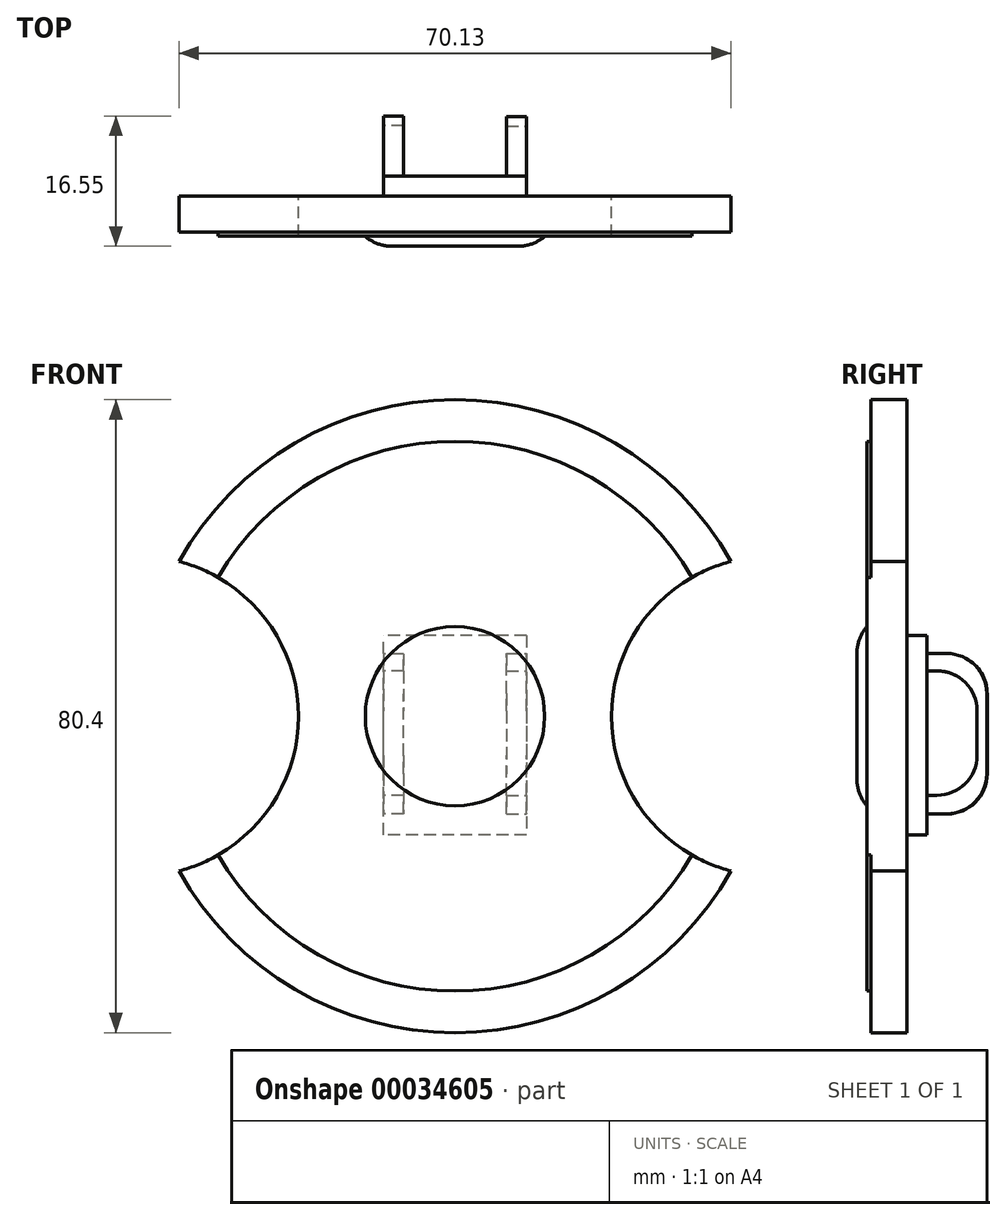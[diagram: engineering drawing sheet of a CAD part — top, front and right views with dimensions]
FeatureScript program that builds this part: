
annotation { "Feature Type Name" : "Feature", "Feature Type Description" : "" }
export const myFeature = defineFeature(function(context is Context, id is Id, definition is map)
    precondition{}
    {
        {
            var Q0;
            Q0=qCreatedBy(makeId("Front.planeOp"),FACE);
            var sketch = newSketch(context, id + "F0", { "sketchPlane" : qUnion([Q0])});
            skArc(sketch, "E0", {"start": v(-64.25, 9.99) * mm, "mid": v(-29.18, -10.55) * mm, "end": v(5.88, 9.99) * mm});
            skArc(sketch, "E1", {"start": v(-64.25, 9.99) * mm, "mid": v(-49.06, 29.65) * mm, "end": v(-64.25, 49.31) * mm});
            skArc(sketch, "E2", {"start": v(5.88, 49.31) * mm, "mid": v(-9.3, 29.65) * mm, "end": v(5.88, 9.99) * mm});
            skCircle(sketch, "E3", {"center": v(-29.18, 29.65) * mm, "radius": 11.4 * mm});
            skArc(sketch, "E4.trimOffspring", {"start": v(5.88, 49.31) * mm, "mid": v(-29.18, 69.85) * mm, "end": v(-64.25, 49.31) * mm});
            skArc(sketch, "E5", {"start": v(-59.31, 12) * mm, "mid": v(-29.18, -5.27) * mm, "end": v(0.94, 12) * mm});
            skArc(sketch, "E6.trimOffspring", {"start": v(0.94, 47.3) * mm, "mid": v(-29.18, 64.57) * mm, "end": v(-59.31, 47.3) * mm});
            skPoint(sketch, "E7.top.end.orphan", {"position": v(-31.2, 43.28) * mm});
            skPoint(sketch, "E8.bottom.start.orphan", {"position": v(-29.18, 43.28) * mm});
            skPoint(sketch, "E9.top.end.orphan", {"position": v(-16.7, 38.94) * mm});
            skPoint(sketch, "E10.bottom.start.orphan", {"position": v(-14.68, 38.94) * mm});
            skSolve(sketch);
        }
        {
            var Q0;
            Q0=makeQuery(id+"F0.imprint","IMPRINT",FACE,{"disambiguationData":[TD([[makeQuery(id+"F0.imprint","IMPRINT",EDGE,{"derivedFrom":sQuery(id+"F0.wireOp",EDGE,"E3")}),1.0]])]});
            extrude(context, id + "F1", {"entities" : qUnion([Q0]), "depth" : 6.35 * mm});
        }
        {
            var Q0;
            Q0=makeQuery(id+"F0.imprint","IMPRINT",FACE,{"disambiguationData":[TD([[makeQuery(id+"F0.imprint","IMPRINT",EDGE,{"derivedFrom":sQuery(id+"F0.wireOp",EDGE,"E3")}),-1.0]])]});
            extrude(context, id + "F2", {"entities" : qUnion([Q0]), "operationType" : NewBodyOperationType.ADD, "depth" : 5.08 * mm});
        }
        {
            var Q0;
            {var subQ1=sQuery(id+"F0.wireOp",EDGE,"E4.trimOffspring");Q0=makeQuery(id+"F0.imprint","IMPRINT",FACE,{"disambiguationData":[TD([[makeQuery(id+"F0.imprint","IMPRINT",EDGE,{"derivedFrom":subQ1}),1.0]])]});}
            var Q1;
            {var subQ2=sQuery(id+"F0.wireOp",EDGE,"E0");Q1=makeQuery(id+"F0.imprint","IMPRINT",FACE,{"disambiguationData":[TD([[makeQuery(id+"F0.imprint","IMPRINT",EDGE,{"derivedFrom":subQ2}),1.0]])]});}
            extrude(context, id + "F3", {"entities" : qUnion([Q0, Q1]), "operationType" : NewBodyOperationType.ADD, "depth" : 4.57 * mm});
        }
        {
            var Q0;
            Q0=makeQuery(id+"F3.opExtrude","CAP_EDGE",EDGE,{"disambiguationData":[OSD([sQuery(id+"F0.wireOp",EDGE,"E6.trimOffspring")])],"isStart":false});
            var Q1;
            Q1=makeQuery(id+"F3.opExtrude","CAP_EDGE",EDGE,{"disambiguationData":[OSD([sQuery(id+"F0.wireOp",EDGE,"E5")])],"isStart":false});
            var Q2;
            Q2=makeQuery(id+"F1.opExtrude","CAP_EDGE",EDGE,{"disambiguationData":[OSD([sQuery(id+"F0.wireOp",EDGE,"E3")])],"isStart":false});
            fillet(context, id + "F4", {"entities" : qUnion([Q0, Q1, Q2]), "radius" : 5.08 * mm, "tangentPropagation" : true, "allowEdgeOverflow" : false});
        }
        {
            var Q0;
            {var subQ0=sQuery(id+"F0.wireOp",EDGE,"E3");var subQ1=sQuery(id+"F0.wireOp",EDGE,"E1");var subQ2=sQuery(id+"F0.wireOp",EDGE,"E2");var subQ3=sQuery(id+"F0.wireOp",EDGE,"E5");var subQ4=sQuery(id+"F0.wireOp",EDGE,"E6.trimOffspring");Q0=makeQuery(id+"F3.boolean.opBoolean","MERGE",FACE,{"derivedFrom":[makeQuery(id+"F2.boolean.opBoolean","MERGE",FACE,{"derivedFrom":[makeQuery(id+"F1.opExtrude","CAP_FACE",FACE,{"disambiguationData":[OSD([subQ0])],"isStart":true}),makeQuery(id+"F2.opExtrude","CAP_FACE",FACE,{"disambiguationData":[OSD([subQ1,subQ2,subQ0,subQ3,subQ4])],"isStart":true})]}),makeQuery(id+"F3.opExtrude","CAP_FACE",FACE,{"disambiguationData":[OSD([sQuery(id+"F0.wireOp",EDGE,"E0"),subQ1,subQ2,subQ3])],"isStart":true}),makeQuery(id+"F3.opExtrude","CAP_FACE",FACE,{"disambiguationData":[OSD([subQ1,subQ2,sQuery(id+"F0.wireOp",EDGE,"E4.trimOffspring"),subQ4])],"isStart":true})]});}
            var sketch = newSketch(context, id + "F5", { "sketchPlane" : qUnion([Q0])});
            skPoint(sketch, "E11.firstSnap0", {"position": v(29.18, -10.55) * mm});
            skLineSegment(sketch, "E11.bottom", {"start": v(29.18, 14.6) * mm, "end": v(38.27, 14.6) * mm});
            skLineSegment(sketch, "E11.left", {"start": v(29.18, 14.6) * mm, "end": v(29.18, 39.9) * mm});
            skLineSegment(sketch, "E11.right", {"start": v(38.27, 14.6) * mm, "end": v(38.27, 39.9) * mm});
            skLineSegment(sketch, "E12.top", {"start": v(29.18, 14.6) * mm, "end": v(20.1, 14.6) * mm});
            skLineSegment(sketch, "E12.left", {"start": v(29.18, 39.9) * mm, "end": v(29.18, 14.6) * mm});
            skLineSegment(sketch, "E12.right", {"start": v(20.1, 39.9) * mm, "end": v(20.1, 14.6) * mm});
            skLineSegment(sketch, "E13", {"start": v(20.1, 39.9) * mm, "end": v(29.18, 39.9) * mm});
            skLineSegment(sketch, "E14", {"start": v(29.18, 39.9) * mm, "end": v(38.27, 39.9) * mm});
            skSolve(sketch);
        }
        {
            var Q0;
            Q0=makeQuery(id+"F5.imprint","IMPRINT",FACE,{"disambiguationData":[TD([[makeQuery(id+"F5.imprint","IMPRINT",EDGE,{"derivedFrom":sQuery(id+"F5.wireOp",EDGE,"E11.bottom")}),1.0]])]});
            extrude(context, id + "F6", {"entities" : qUnion([Q0]), "operationType" : NewBodyOperationType.ADD, "depth" : 2.54 * mm});
        }
        {
            var Q0;
            Q0=makeQuery(id+"F5.imprint","IMPRINT",FACE,{"disambiguationData":[TD([[makeQuery(id+"F5.imprint","IMPRINT",EDGE,{"derivedFrom":sQuery(id+"F5.wireOp",EDGE,"E12.top")}),-1.0]])]});
            extrude(context, id + "F7", {"entities" : qUnion([Q0]), "operationType" : NewBodyOperationType.ADD, "depth" : 2.54 * mm});
        }
        {
            var Q0;
            Q0=makeQuery(id+"F6.opExtrude","SWEPT_FACE",FACE,{"disambiguationData":[OSD([sQuery(id+"F5.wireOp",EDGE,"E11.right")])]});
            var sketch = newSketch(context, id + "F8", { "sketchPlane" : qUnion([Q0])});
            skLineSegment(sketch, "E15.bottom", {"start": v(-2.54, 17.24) * mm, "end": v(-10.2, 17.24) * mm});
            skLineSegment(sketch, "E15.top", {"start": v(-2.54, 37.59) * mm, "end": v(-10.2, 37.59) * mm});
            skLineSegment(sketch, "E15.left", {"start": v(-2.54, 17.24) * mm, "end": v(-2.54, 37.59) * mm});
            skLineSegment(sketch, "E15.right", {"start": v(-10.2, 17.24) * mm, "end": v(-10.2, 37.59) * mm});
            skLineSegment(sketch, "E16.bottom", {"start": v(-2.54, 19.59) * mm, "end": v(-8.97, 19.59) * mm});
            skLineSegment(sketch, "E16.top", {"start": v(-2.54, 35.39) * mm, "end": v(-8.97, 35.39) * mm});
            skLineSegment(sketch, "E16.left", {"start": v(-2.54, 19.59) * mm, "end": v(-2.54, 35.39) * mm});
            skLineSegment(sketch, "E16.right", {"start": v(-8.97, 19.59) * mm, "end": v(-8.97, 35.39) * mm});
            skSolve(sketch);
        }
        {
            var Q0;
            Q0=makeQuery(id+"F7.opExtrude","SWEPT_FACE",FACE,{"disambiguationData":[OSD([sQuery(id+"F5.wireOp",EDGE,"E12.right")])]});
            var sketch = newSketch(context, id + "F9", { "sketchPlane" : qUnion([Q0])});
            skLineSegment(sketch, "E17.bottom", {"start": v(10.13, 37.62) * mm, "end": v(2.54, 37.62) * mm});
            skLineSegment(sketch, "E17.top", {"start": v(8.9, 35.42) * mm, "end": v(2.54, 35.42) * mm});
            skLineSegment(sketch, "E17.left", {"start": v(10.13, 37.62) * mm, "end": v(10.13, 35.42) * mm});
            skLineSegment(sketch, "E17.right", {"start": v(2.54, 37.62) * mm, "end": v(2.54, 35.42) * mm});
            skLineSegment(sketch, "E18.top", {"start": v(8.9, 17.26) * mm, "end": v(10.13, 17.26) * mm});
            skLineSegment(sketch, "E18.left", {"start": v(8.9, 35.42) * mm, "end": v(8.9, 19.6) * mm});
            skLineSegment(sketch, "E18.right", {"start": v(10.13, 35.42) * mm, "end": v(10.13, 17.26) * mm});
            skLineSegment(sketch, "E19.bottom", {"start": v(8.9, 17.26) * mm, "end": v(2.54, 17.26) * mm});
            skLineSegment(sketch, "E19.top", {"start": v(8.9, 19.6) * mm, "end": v(2.54, 19.6) * mm});
            skLineSegment(sketch, "E19.right", {"start": v(2.54, 17.26) * mm, "end": v(2.54, 19.6) * mm});
            skSolve(sketch);
        }
        {
            var Q0;
            Q0 = qSketchRegion(id + "F9", true);
            extrude(context, id + "F10", {"entities" : qUnion([Q0]), "oppositeDirection" : true, "depth" : 2.54 * mm});
        }
        {
            var Q0;
            {var subQ6=sQuery(id+"F8.wireOp",EDGE,"E15.bottom");Q0=makeQuery(id+"F8.imprint","IMPRINT",FACE,{"disambiguationData":[TD([[makeQuery(id+"F8.imprint","IMPRINT",EDGE,{"derivedFrom":subQ6}),-1.0]])]});}
            extrude(context, id + "F11", {"entities" : qUnion([Q0]), "oppositeDirection" : true, "depth" : 2.54 * mm});
        }
        {
            var Q0;
            Q0=makeQuery(id+"F7.boolean.opBoolean","MERGE",EDGE,{"derivedFrom":[makeQuery(id+"F6.opExtrude","CAP_EDGE",EDGE,{"disambiguationData":[OSD([sQuery(id+"F5.wireOp",EDGE,"E14")])],"isStart":true}),makeQuery(id+"F7.opExtrude","CAP_EDGE",EDGE,{"disambiguationData":[OSD([sQuery(id+"F5.wireOp",EDGE,"E13")])],"isStart":true})]});
            var Q1;
            Q1=makeQuery(id+"F7.boolean.opBoolean","MERGE",EDGE,{"derivedFrom":[makeQuery(id+"F6.opExtrude","CAP_EDGE",EDGE,{"disambiguationData":[OSD([sQuery(id+"F5.wireOp",EDGE,"E11.bottom")])],"isStart":true}),makeQuery(id+"F7.opExtrude","CAP_EDGE",EDGE,{"disambiguationData":[OSD([sQuery(id+"F5.wireOp",EDGE,"E12.top")])],"isStart":true})]});
            var Q2;
            Q2=makeQuery(id+"F7.opExtrude","CAP_EDGE",EDGE,{"disambiguationData":[OSD([sQuery(id+"F5.wireOp",EDGE,"E12.right")])],"isStart":true});
            var Q3;
            Q3=makeQuery(id+"F6.opExtrude","CAP_EDGE",EDGE,{"disambiguationData":[OSD([sQuery(id+"F5.wireOp",EDGE,"E11.right")])],"isStart":true});
            var Q4;
            Q4=makeQuery(id+"F11.opExtrude","SWEPT_EDGE",EDGE,{"disambiguationData":[OSD([sQuery(id+"F8.wireOp",EDGE,"E15.bottom"),sQuery(id+"F8.wireOp",EDGE,"E15.right")])]});
            var Q5;
            Q5=makeQuery(id+"F11.opExtrude","SWEPT_EDGE",EDGE,{"disambiguationData":[OSD([sQuery(id+"F8.wireOp",EDGE,"E15.top"),sQuery(id+"F8.wireOp",EDGE,"E15.right")])]});
            var Q6;
            Q6=makeQuery(id+"F10.opExtrude","SWEPT_EDGE",EDGE,{"disambiguationData":[OSD([sQuery(id+"F9.wireOp",EDGE,"E18.top"),sQuery(id+"F9.wireOp",EDGE,"E18.right")])]});
            var Q7;
            Q7=makeQuery(id+"F10.opExtrude","SWEPT_EDGE",EDGE,{"disambiguationData":[OSD([sQuery(id+"F9.wireOp",EDGE,"E17.bottom"),sQuery(id+"F9.wireOp",EDGE,"E17.left")])]});
            var Q8;
            Q8=makeQuery(id+"F11.opExtrude","SWEPT_EDGE",EDGE,{"disambiguationData":[OSD([sQuery(id+"F8.wireOp",EDGE,"E16.top"),sQuery(id+"F8.wireOp",EDGE,"E16.right")])]});
            var Q9;
            Q9=makeQuery(id+"F11.opExtrude","SWEPT_EDGE",EDGE,{"disambiguationData":[OSD([sQuery(id+"F8.wireOp",EDGE,"E16.bottom"),sQuery(id+"F8.wireOp",EDGE,"E16.right")])]});
            var Q10;
            Q10=makeQuery(id+"F10.opExtrude","SWEPT_EDGE",EDGE,{"disambiguationData":[OSD([sQuery(id+"F9.wireOp",EDGE,"E17.top"),sQuery(id+"F9.wireOp",EDGE,"E18.left")])]});
            var Q11;
            Q11=makeQuery(id+"F10.opExtrude","SWEPT_EDGE",EDGE,{"disambiguationData":[OSD([sQuery(id+"F9.wireOp",EDGE,"E18.left"),sQuery(id+"F9.wireOp",EDGE,"E19.top")])]});
            fillet(context, id + "F12", {"entities" : qUnion([Q0, Q1, Q2, Q3, Q4, Q5, Q6, Q7, Q8, Q9, Q10, Q11]), "radius" : 5.08 * mm, "tangentPropagation" : true, "allowEdgeOverflow" : false});
        }
    });
